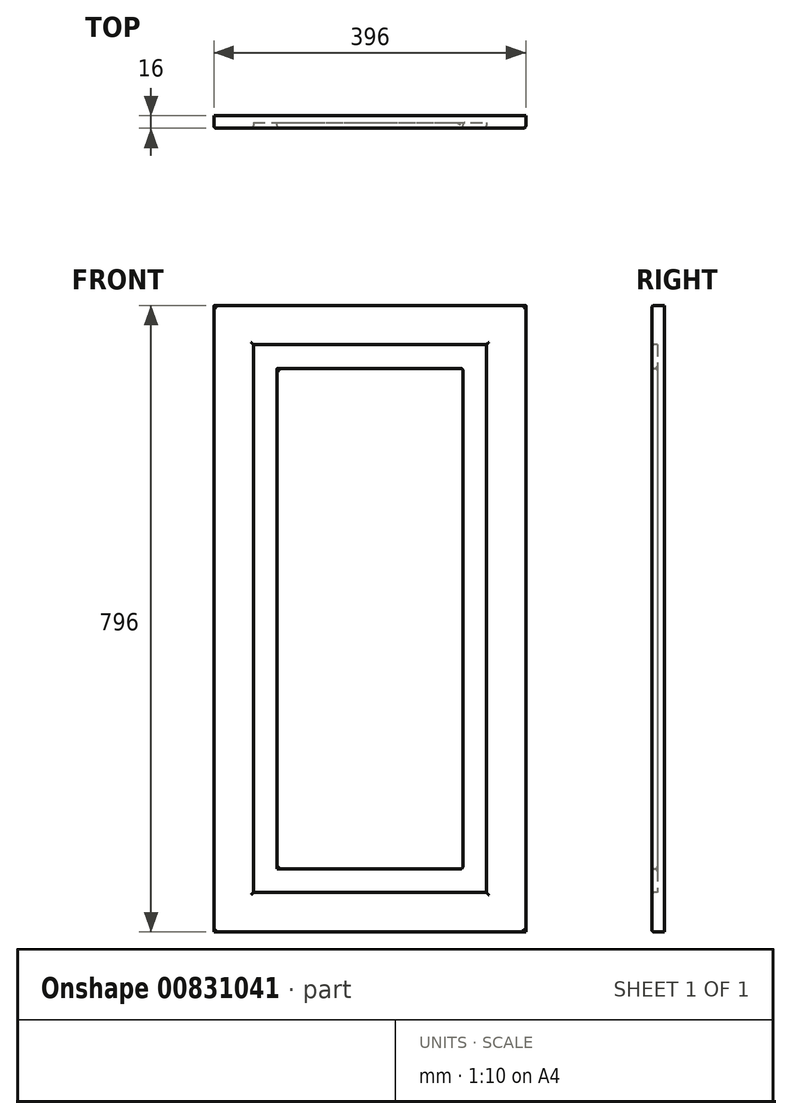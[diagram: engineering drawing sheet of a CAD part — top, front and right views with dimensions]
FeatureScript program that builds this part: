
annotation { "Feature Type Name" : "Feature", "Feature Type Description" : "" }
export const myFeature = defineFeature(function(context is Context, id is Id, definition is map)
    precondition{}
    {
        {
            var Q0;
            Q0=qCreatedBy(makeId("Front.planeOp"),FACE);
            var sketch = newSketch(context, id + "F0", { "sketchPlane" : qUnion([Q0])});
            skLineSegment(sketch, "E0.bottom", {"start": v(0, 0) * mm, "end": v(44.66, 0) * mm});
            skLineSegment(sketch, "E0.top", {"start": v(0, 33.8) * mm, "end": v(44.66, 33.8) * mm});
            skLineSegment(sketch, "E0.left", {"start": v(0, 0) * mm, "end": v(0, 33.8) * mm});
            skLineSegment(sketch, "E0.right", {"start": v(44.66, 0) * mm, "end": v(44.66, 33.8) * mm});
            skSolve(sketch);
        }
        {
            var Q0;
            Q0=makeQuery(id+"F0.imprint","IMPRINT",FACE,{"disambiguationData":[TD([[makeQuery(id+"F0.imprint","IMPRINT",EDGE,{"derivedFrom":sQuery(id+"F0.wireOp",EDGE,"E0.bottom")}),1.0]])]});
            extrude(context, id + "F1", {"entities" : qUnion([Q0]), "depth" : 16 * mm, "offsetDistance" : 25.4 * mm});
        }
        {
            var Q0;
            Q0=makeQuery(id+"F1.opExtrude","SWEPT_FACE",FACE,{"disambiguationData":[OSD([sQuery(id+"F0.wireOp",EDGE,"E0.bottom")])]});
            extrude(context, id + "F2", {"entities" : qUnion([Q0]), "operationType" : NewBodyOperationType.ADD, "oppositeDirection" : true, "depth" : 796 * mm, "offsetDistance" : 25 * mm});
        }
        {
            var Q0;
            {var subQ0=sQuery(id+"F0.wireOp",EDGE,"E0.left");Q0=makeQuery(id+"F2.boolean.opBoolean","MERGE",FACE,{"derivedFrom":[makeQuery(id+"F1.opExtrude","SWEPT_FACE",FACE,{"disambiguationData":[OSD([subQ0])]}),makeQuery(id+"F2.opExtrude","SWEPT_FACE",FACE,{"disambiguationData":[OSD([sQuery(id+"F0.wireOp",EDGE,"E0.bottom"),subQ0])]})]});}
            extrude(context, id + "F3", {"entities" : qUnion([Q0]), "operationType" : NewBodyOperationType.ADD, "oppositeDirection" : true, "depth" : 196 * mm, "offsetDistance" : 25 * mm});
        }
        {
            var Q0;
            {var subQ0=sQuery(id+"F0.wireOp",EDGE,"E0.left");var subQ1=sQuery(id+"F0.wireOp",EDGE,"E0.bottom");Q0=makeQuery(id+"F3.boolean.opBoolean","MERGE",FACE,{"derivedFrom":[makeQuery(id+"F2.boolean.opBoolean","MERGE",FACE,{"derivedFrom":[makeQuery(id+"F1.opExtrude","CAP_FACE",FACE,{"disambiguationData":[OSD([subQ1,sQuery(id+"F0.wireOp",EDGE,"E0.top"),subQ0,sQuery(id+"F0.wireOp",EDGE,"E0.right")])],"isStart":false}),makeQuery(id+"F2.opExtrude","SWEPT_FACE",FACE,{"disambiguationData":[OSD([subQ1]),TDD([makeQuery(id+"F1.opExtrude","CAP_EDGE",EDGE,{"disambiguationData":[OSD([subQ1])],"isStart":false})])]})]}),makeQuery(id+"F3.opExtrude","SWEPT_FACE",FACE,{"disambiguationData":[OSD([subQ1,subQ0]),TDD([makeQuery(id+"F2.boolean.opBoolean","MERGE",EDGE,{"derivedFrom":[makeQuery(id+"F1.opExtrude","CAP_EDGE",EDGE,{"disambiguationData":[OSD([subQ0])],"isStart":false}),makeQuery(id+"F2.opExtrude","SWEPT_EDGE",EDGE,{"disambiguationData":[OSD([subQ1,subQ0]),TDD([makeQuery(id+"F1.opExtrude","CAP_VERTEX",VERTEX,{"disambiguationData":[OSD([subQ1,subQ0])],"isStart":false})])]})]})])]})]});}
            var sketch = newSketch(context, id + "F4", { "sketchPlane" : qUnion([Q0])});
            skLineSegment(sketch, "E1.bottom", {"start": v(59.7, 646.67) * mm, "end": v(128.66, 646.67) * mm});
            skLineSegment(sketch, "E1.top", {"start": v(59.7, 152.97) * mm, "end": v(128.66, 152.97) * mm});
            skLineSegment(sketch, "E1.left", {"start": v(59.7, 646.67) * mm, "end": v(59.7, 152.97) * mm});
            skLineSegment(sketch, "E1.right", {"start": v(128.66, 646.67) * mm, "end": v(128.66, 152.97) * mm});
            skSolve(sketch);
        }
        {
            var Q0;
            Q0=makeQuery(id+"F4.imprint","IMPRINT",FACE,{"disambiguationData":[TD([[makeQuery(id+"F4.imprint","IMPRINT",EDGE,{"derivedFrom":sQuery(id+"F4.wireOp",EDGE,"E1.bottom")}),-1.0]])]});
            extrude(context, id + "F5", {"entities" : qUnion([Q0]), "operationType" : NewBodyOperationType.REMOVE, "oppositeDirection" : true, "depth" : 7 * mm, "offsetDistance" : 25 * mm});
        }
        {
            var Q0;
            Q0=makeQuery(id+"F5.boolean.opBoolean","COPY",FACE,{"derivedFrom":makeQuery(id+"F5.opExtrude","SWEPT_FACE",FACE,{"disambiguationData":[OSD([sQuery(id+"F4.wireOp",EDGE,"E1.left")])]})});
            extrude(context, id + "F6", {"entities" : qUnion([Q0]), "operationType" : NewBodyOperationType.REMOVE, "oppositeDirection" : true, "depth" : 9.7 * mm, "offsetDistance" : 25 * mm});
        }
        {
            var Q0;
            {var subQ0=sQuery(id+"F4.wireOp",EDGE,"E1.bottom");Q0=makeQuery(id+"F6.boolean.opBoolean","MERGE",FACE,{"derivedFrom":[makeQuery(id+"F5.boolean.opBoolean","COPY",FACE,{"derivedFrom":makeQuery(id+"F5.opExtrude","SWEPT_FACE",FACE,{"disambiguationData":[OSD([subQ0])]})}),makeQuery(id+"F6.opExtrude","SWEPT_FACE",FACE,{"disambiguationData":[OSD([subQ0,sQuery(id+"F4.wireOp",EDGE,"E1.left")])]})]});}
            extrude(context, id + "F7", {"entities" : qUnion([Q0]), "operationType" : NewBodyOperationType.ADD, "oppositeDirection" : true, "depth" : 99.33 * mm, "offsetDistance" : 25 * mm});
        }
        {
            var Q0;
            {var subQ0=sQuery(id+"F4.wireOp",EDGE,"E1.bottom");Q0=makeQuery(id+"F6.boolean.opBoolean","MERGE",FACE,{"derivedFrom":[makeQuery(id+"F5.boolean.opBoolean","COPY",FACE,{"derivedFrom":makeQuery(id+"F5.opExtrude","SWEPT_FACE",FACE,{"disambiguationData":[OSD([subQ0])]})}),makeQuery(id+"F6.opExtrude","SWEPT_FACE",FACE,{"disambiguationData":[OSD([subQ0,sQuery(id+"F4.wireOp",EDGE,"E1.left")])]})]});}
            extrude(context, id + "F8", {"entities" : qUnion([Q0]), "operationType" : NewBodyOperationType.REMOVE, "oppositeDirection" : true, "depth" : 99.33 * mm, "offsetDistance" : 25 * mm});
        }
        {
            var Q0;
            {var subQ0=sQuery(id+"F4.wireOp",EDGE,"E1.right");Q0=makeQuery(id+"F8.boolean.opBoolean","MERGE",FACE,{"derivedFrom":[makeQuery(id+"F5.boolean.opBoolean","COPY",FACE,{"derivedFrom":makeQuery(id+"F5.opExtrude","SWEPT_FACE",FACE,{"disambiguationData":[OSD([subQ0])]})}),makeQuery(id+"F8.opExtrude","SWEPT_FACE",FACE,{"disambiguationData":[OSD([sQuery(id+"F4.wireOp",EDGE,"E1.bottom"),subQ0])]})]});}
            extrude(context, id + "F9", {"entities" : qUnion([Q0]), "operationType" : NewBodyOperationType.REMOVE, "oppositeDirection" : true, "depth" : 17.34 * mm, "offsetDistance" : 25 * mm});
        }
        {
            var Q0;
            {var subQ0=sQuery(id+"F4.wireOp",EDGE,"E1.top");Q0=makeQuery(id+"F9.boolean.opBoolean","MERGE",FACE,{"derivedFrom":[makeQuery(id+"F6.boolean.opBoolean","MERGE",FACE,{"derivedFrom":[makeQuery(id+"F5.boolean.opBoolean","COPY",FACE,{"derivedFrom":makeQuery(id+"F5.opExtrude","SWEPT_FACE",FACE,{"disambiguationData":[OSD([subQ0])]})}),makeQuery(id+"F6.opExtrude","SWEPT_FACE",FACE,{"disambiguationData":[OSD([subQ0,sQuery(id+"F4.wireOp",EDGE,"E1.left")])]})]}),makeQuery(id+"F9.opExtrude","SWEPT_FACE",FACE,{"disambiguationData":[OSD([subQ0,sQuery(id+"F4.wireOp",EDGE,"E1.right")])]})]});}
            extrude(context, id + "F10", {"entities" : qUnion([Q0]), "operationType" : NewBodyOperationType.REMOVE, "oppositeDirection" : true, "depth" : 102.97 * mm, "offsetDistance" : 25 * mm});
        }
        {
            var Q0;
            {var subQ0=sQuery(id+"F4.wireOp",EDGE,"E1.right");var subQ1=sQuery(id+"F4.wireOp",EDGE,"E1.top");var subQ2=sQuery(id+"F4.wireOp",EDGE,"E1.left");var subQ3=sQuery(id+"F4.wireOp",EDGE,"E1.bottom");Q0=makeQuery(id+"F10.boolean.opBoolean","MERGE",FACE,{"derivedFrom":[makeQuery(id+"F9.boolean.opBoolean","MERGE",FACE,{"derivedFrom":[makeQuery(id+"F8.boolean.opBoolean","MERGE",FACE,{"derivedFrom":[makeQuery(id+"F6.boolean.opBoolean","MERGE",FACE,{"derivedFrom":[makeQuery(id+"F5.boolean.opBoolean","COPY",FACE,{"derivedFrom":makeQuery(id+"F5.opExtrude","CAP_FACE",FACE,{"disambiguationData":[OSD([subQ3,subQ1,subQ2,subQ0])],"isStart":false})}),makeQuery(id+"F6.opExtrude","SWEPT_FACE",FACE,{"disambiguationData":[OSD([subQ2]),TDD([makeQuery(id+"F5.boolean.opBoolean","COPY",EDGE,{"derivedFrom":makeQuery(id+"F5.opExtrude","CAP_EDGE",EDGE,{"disambiguationData":[OSD([subQ2])],"isStart":false})})])]})]}),makeQuery(id+"F8.opExtrude","SWEPT_FACE",FACE,{"disambiguationData":[OSD([subQ3,subQ2]),TDD([makeQuery(id+"F6.boolean.opBoolean","MERGE",EDGE,{"derivedFrom":[makeQuery(id+"F5.boolean.opBoolean","COPY",EDGE,{"derivedFrom":makeQuery(id+"F5.opExtrude","CAP_EDGE",EDGE,{"disambiguationData":[OSD([subQ3])],"isStart":false})}),makeQuery(id+"F6.opExtrude","SWEPT_EDGE",EDGE,{"disambiguationData":[OSD([subQ3,subQ2]),TDD([makeQuery(id+"F5.boolean.opBoolean","COPY",VERTEX,{"derivedFrom":makeQuery(id+"F5.opExtrude","CAP_VERTEX",VERTEX,{"disambiguationData":[OSD([subQ3,subQ2])],"isStart":false})})])]})]})])]})]}),makeQuery(id+"F9.opExtrude","SWEPT_FACE",FACE,{"disambiguationData":[OSD([subQ3,subQ0]),TDD([makeQuery(id+"F8.boolean.opBoolean","MERGE",EDGE,{"derivedFrom":[makeQuery(id+"F5.boolean.opBoolean","COPY",EDGE,{"derivedFrom":makeQuery(id+"F5.opExtrude","CAP_EDGE",EDGE,{"disambiguationData":[OSD([subQ0])],"isStart":false})}),makeQuery(id+"F8.opExtrude","SWEPT_EDGE",EDGE,{"disambiguationData":[OSD([subQ3,subQ0]),TDD([makeQuery(id+"F5.boolean.opBoolean","COPY",VERTEX,{"derivedFrom":makeQuery(id+"F5.opExtrude","CAP_VERTEX",VERTEX,{"disambiguationData":[OSD([subQ3,subQ0])],"isStart":false})})])]})]})])]})]}),makeQuery(id+"F10.opExtrude","SWEPT_FACE",FACE,{"disambiguationData":[OSD([subQ1,subQ2,subQ0]),TDD([makeQuery(id+"F9.boolean.opBoolean","MERGE",EDGE,{"derivedFrom":[makeQuery(id+"F6.boolean.opBoolean","MERGE",EDGE,{"derivedFrom":[makeQuery(id+"F5.boolean.opBoolean","COPY",EDGE,{"derivedFrom":makeQuery(id+"F5.opExtrude","CAP_EDGE",EDGE,{"disambiguationData":[OSD([subQ1])],"isStart":false})}),makeQuery(id+"F6.opExtrude","SWEPT_EDGE",EDGE,{"disambiguationData":[OSD([subQ1,subQ2]),TDD([makeQuery(id+"F5.boolean.opBoolean","COPY",VERTEX,{"derivedFrom":makeQuery(id+"F5.opExtrude","CAP_VERTEX",VERTEX,{"disambiguationData":[OSD([subQ1,subQ2])],"isStart":false})})])]})]}),makeQuery(id+"F9.opExtrude","SWEPT_EDGE",EDGE,{"disambiguationData":[OSD([subQ1,subQ0]),TDD([makeQuery(id+"F5.boolean.opBoolean","COPY",VERTEX,{"derivedFrom":makeQuery(id+"F5.opExtrude","CAP_VERTEX",VERTEX,{"disambiguationData":[OSD([subQ1,subQ0])],"isStart":false})})])]})]})])]})]});}
            var sketch = newSketch(context, id + "F11", { "sketchPlane" : qUnion([Q0])});
            skLineSegment(sketch, "E2.bottom", {"start": v(74.13, 678.73) * mm, "end": v(109.41, 678.73) * mm});
            skLineSegment(sketch, "E2.top", {"start": v(74.13, 186.63) * mm, "end": v(109.41, 186.63) * mm});
            skLineSegment(sketch, "E2.left", {"start": v(74.13, 678.73) * mm, "end": v(74.13, 186.63) * mm});
            skLineSegment(sketch, "E2.right", {"start": v(109.41, 678.73) * mm, "end": v(109.41, 186.63) * mm});
            skSolve(sketch);
        }
        {
            var Q0;
            Q0=makeQuery(id+"F11.imprint","IMPRINT",FACE,{"disambiguationData":[TD([[makeQuery(id+"F11.imprint","IMPRINT",EDGE,{"derivedFrom":sQuery(id+"F11.wireOp",EDGE,"E2.bottom")}),-1.0]])]});
            extrude(context, id + "F12", {"entities" : qUnion([Q0]), "operationType" : NewBodyOperationType.ADD, "depth" : 7 * mm, "offsetDistance" : 25 * mm});
        }
        {
            var Q0;
            Q0=makeQuery(id+"F12.opExtrude","SWEPT_FACE",FACE,{"disambiguationData":[OSD([sQuery(id+"F11.wireOp",EDGE,"E2.bottom")])]});
            extrude(context, id + "F13", {"entities" : qUnion([Q0]), "operationType" : NewBodyOperationType.ADD, "depth" : 37.27 * mm, "offsetDistance" : 25 * mm});
        }
        {
            var Q0;
            {var subQ0=sQuery(id+"F11.wireOp",EDGE,"E2.right");Q0=makeQuery(id+"F13.boolean.opBoolean","MERGE",FACE,{"derivedFrom":[makeQuery(id+"F12.opExtrude","SWEPT_FACE",FACE,{"disambiguationData":[OSD([subQ0])]}),makeQuery(id+"F13.opExtrude","SWEPT_FACE",FACE,{"disambiguationData":[OSD([sQuery(id+"F11.wireOp",EDGE,"E2.bottom"),subQ0])]})]});}
            extrude(context, id + "F14", {"entities" : qUnion([Q0]), "operationType" : NewBodyOperationType.ADD, "depth" : 6.58 * mm, "offsetDistance" : 25 * mm});
        }
        {
            var Q0;
            {var subQ0=sQuery(id+"F11.wireOp",EDGE,"E2.top");Q0=makeQuery(id+"F14.boolean.opBoolean","MERGE",FACE,{"derivedFrom":[makeQuery(id+"F12.opExtrude","SWEPT_FACE",FACE,{"disambiguationData":[OSD([subQ0])]}),makeQuery(id+"F14.opExtrude","SWEPT_FACE",FACE,{"disambiguationData":[OSD([subQ0,sQuery(id+"F11.wireOp",EDGE,"E2.right")])]})]});}
            extrude(context, id + "F15", {"entities" : qUnion([Q0]), "operationType" : NewBodyOperationType.ADD, "depth" : 106.63 * mm, "offsetDistance" : 25 * mm});
        }
        {
            var Q0;
            {var subQ0=sQuery(id+"F11.wireOp",EDGE,"E2.left");Q0=makeQuery(id+"F15.boolean.opBoolean","MERGE",FACE,{"derivedFrom":[makeQuery(id+"F13.boolean.opBoolean","MERGE",FACE,{"derivedFrom":[makeQuery(id+"F12.opExtrude","SWEPT_FACE",FACE,{"disambiguationData":[OSD([subQ0])]}),makeQuery(id+"F13.opExtrude","SWEPT_FACE",FACE,{"disambiguationData":[OSD([sQuery(id+"F11.wireOp",EDGE,"E2.bottom"),subQ0])]})]}),makeQuery(id+"F15.opExtrude","SWEPT_FACE",FACE,{"disambiguationData":[OSD([sQuery(id+"F11.wireOp",EDGE,"E2.top"),subQ0])]})]});}
            extrude(context, id + "F16", {"entities" : qUnion([Q0]), "operationType" : NewBodyOperationType.REMOVE, "oppositeDirection" : true, "depth" : 5.87 * mm, "offsetDistance" : 25 * mm});
        }
        {
            var Q0;
            Q0=makeQuery(id+"F3.opExtrude","CAP_FACE",FACE,{"disambiguationData":[OSD([sQuery(id+"F0.wireOp",EDGE,"E0.bottom"),sQuery(id+"F0.wireOp",EDGE,"E0.left")])],"isStart":false});
            extrude(context, id + "F17", {"entities" : qUnion([Q0]), "operationType" : NewBodyOperationType.ADD, "depth" : 200 * mm, "offsetDistance" : 25 * mm});
        }
        {
            var Q0;
            {var subQ0=sQuery(id+"F4.wireOp",EDGE,"E1.right");Q0=makeQuery(id+"F10.boolean.opBoolean","MERGE",FACE,{"derivedFrom":[makeQuery(id+"F9.boolean.opBoolean","COPY",FACE,{"derivedFrom":makeQuery(id+"F9.opExtrude","CAP_FACE",FACE,{"disambiguationData":[OSD([sQuery(id+"F4.wireOp",EDGE,"E1.bottom"),subQ0])],"isStart":false})}),makeQuery(id+"F10.opExtrude","SWEPT_FACE",FACE,{"disambiguationData":[OSD([sQuery(id+"F4.wireOp",EDGE,"E1.top"),subQ0])]})]});}
            extrude(context, id + "F18", {"entities" : qUnion([Q0]), "operationType" : NewBodyOperationType.REMOVE, "oppositeDirection" : true, "depth" : 200 * mm, "offsetDistance" : 25 * mm});
        }
        {
            var Q0;
            {var subQ0=sQuery(id+"F11.wireOp",EDGE,"E2.right");var subQ1=sQuery(id+"F11.wireOp",EDGE,"E2.top");Q0=makeQuery(id+"F15.boolean.opBoolean","MERGE",FACE,{"derivedFrom":[makeQuery(id+"F14.opExtrude","CAP_FACE",FACE,{"disambiguationData":[OSD([sQuery(id+"F11.wireOp",EDGE,"E2.bottom"),subQ0])],"isStart":false}),makeQuery(id+"F15.opExtrude","SWEPT_FACE",FACE,{"disambiguationData":[OSD([subQ1,subQ0]),TDD([makeQuery(id+"F14.opExtrude","CAP_EDGE",EDGE,{"disambiguationData":[OSD([subQ1,subQ0])],"isStart":false})])]})]});}
            extrude(context, id + "F19", {"entities" : qUnion([Q0]), "operationType" : NewBodyOperationType.ADD, "depth" : 200 * mm, "offsetDistance" : 25 * mm});
        }
        {
            var Q0;
            {var subQ0=sQuery(id+"F11.wireOp",EDGE,"E2.right");var subQ1=sQuery(id+"F11.wireOp",EDGE,"E2.top");Q0=makeQuery(id+"F19.boolean.opBoolean","MERGE",FACE,{"derivedFrom":[makeQuery(id+"F15.opExtrude","CAP_FACE",FACE,{"disambiguationData":[OSD([subQ1,subQ0])],"isStart":false}),makeQuery(id+"F19.opExtrude","SWEPT_FACE",FACE,{"disambiguationData":[OSD([subQ1,subQ0])]})]});}
            extrude(context, id + "F20", {"entities" : qUnion([Q0]), "operationType" : NewBodyOperationType.REMOVE, "oppositeDirection" : true, "depth" : 600 * mm, "offsetDistance" : 25 * mm});
        }
        {
            var Q0;
            {var subQ0=sQuery(id+"F4.wireOp",EDGE,"E1.right");var subQ1=sQuery(id+"F4.wireOp",EDGE,"E1.top");Q0=makeQuery(id+"F18.boolean.opBoolean","MERGE",FACE,{"derivedFrom":[makeQuery(id+"F10.boolean.opBoolean","COPY",FACE,{"derivedFrom":makeQuery(id+"F10.opExtrude","CAP_FACE",FACE,{"disambiguationData":[OSD([subQ1,sQuery(id+"F4.wireOp",EDGE,"E1.left"),subQ0])],"isStart":false})}),makeQuery(id+"F18.opExtrude","SWEPT_FACE",FACE,{"disambiguationData":[OSD([subQ1,subQ0])]})]});}
            extrude(context, id + "F21", {"entities" : qUnion([Q0]), "operationType" : NewBodyOperationType.ADD, "depth" : 600 * mm, "offsetDistance" : 25 * mm});
        }
        {
            var Q0;
            {var subQ0=sQuery(id+"F0.wireOp",EDGE,"E0.left");var subQ1=sQuery(id+"F0.wireOp",EDGE,"E0.bottom");var subQ2=makeQuery(id+"F1.opExtrude","SWEPT_EDGE",EDGE,{"disambiguationData":[OSD([subQ1,subQ0])]});Q0=makeQuery(id+"F17.boolean.opBoolean","MERGE",FACE,{"derivedFrom":[makeQuery(id+"F3.boolean.opBoolean","MERGE",FACE,{"derivedFrom":[makeQuery(id+"F1.opExtrude","SWEPT_FACE",FACE,{"disambiguationData":[OSD([subQ1])]}),makeQuery(id+"F3.opExtrude","SWEPT_FACE",FACE,{"disambiguationData":[OSD([subQ1,subQ0]),TDD([subQ2])]})]}),makeQuery(id+"F17.opExtrude","SWEPT_FACE",FACE,{"disambiguationData":[OSD([subQ1,subQ0]),TDD([makeQuery(id+"F3.opExtrude","CAP_EDGE",EDGE,{"disambiguationData":[OSD([subQ1,subQ0]),TDD([subQ2])],"isStart":false})])]})]});}
            extrude(context, id + "F22", {"entities" : qUnion([Q0]), "operationType" : NewBodyOperationType.REMOVE, "oppositeDirection" : true, "depth" : 600 * mm, "offsetDistance" : 25 * mm});
        }
        {
            var Q0;
            Q0=makeQuery(id+"F22.boolean.opBoolean","COPY",FACE,{"derivedFrom":makeQuery(id+"F22.opExtrude","CAP_FACE",FACE,{"disambiguationData":[OSD([sQuery(id+"F0.wireOp",EDGE,"E0.bottom"),sQuery(id+"F0.wireOp",EDGE,"E0.left")])],"isStart":false})});
            extrude(context, id + "F23", {"entities" : qUnion([Q0]), "operationType" : NewBodyOperationType.ADD, "depth" : 200 * mm, "offsetDistance" : 25 * mm});
        }
        {
            var Q0;
            Q0=makeQuery(id+"F21.opExtrude","CAP_FACE",FACE,{"disambiguationData":[OSD([sQuery(id+"F4.wireOp",EDGE,"E1.top"),sQuery(id+"F4.wireOp",EDGE,"E1.left"),sQuery(id+"F4.wireOp",EDGE,"E1.right")])],"isStart":false});
            extrude(context, id + "F24", {"entities" : qUnion([Q0]), "operationType" : NewBodyOperationType.REMOVE, "oppositeDirection" : true, "depth" : 200 * mm, "offsetDistance" : 25 * mm});
        }
        {
            var Q0;
            Q0=makeQuery(id+"F20.boolean.opBoolean","COPY",FACE,{"derivedFrom":makeQuery(id+"F20.opExtrude","CAP_FACE",FACE,{"disambiguationData":[OSD([sQuery(id+"F11.wireOp",EDGE,"E2.top"),sQuery(id+"F11.wireOp",EDGE,"E2.right")])],"isStart":false})});
            extrude(context, id + "F25", {"entities" : qUnion([Q0]), "operationType" : NewBodyOperationType.ADD, "depth" : 200 * mm, "offsetDistance" : 25 * mm});
        }
        {
            var Q0;
            {var subQ0=sQuery(id+"F0.wireOp",EDGE,"E0.left");var subQ1=sQuery(id+"F0.wireOp",EDGE,"E0.bottom");var subQ2=makeQuery(id+"F2.opExtrude","CAP_EDGE",EDGE,{"disambiguationData":[OSD([subQ1,subQ0])],"isStart":false});Q0=makeQuery(id+"F17.boolean.opBoolean","MERGE",FACE,{"derivedFrom":[makeQuery(id+"F3.boolean.opBoolean","MERGE",FACE,{"derivedFrom":[makeQuery(id+"F2.opExtrude","CAP_FACE",FACE,{"disambiguationData":[OSD([subQ1])],"isStart":false}),makeQuery(id+"F3.opExtrude","SWEPT_FACE",FACE,{"disambiguationData":[OSD([subQ1,subQ0]),TDD([subQ2])]})]}),makeQuery(id+"F17.opExtrude","SWEPT_FACE",FACE,{"disambiguationData":[OSD([subQ1,subQ0]),TDD([makeQuery(id+"F3.opExtrude","CAP_EDGE",EDGE,{"disambiguationData":[OSD([subQ1,subQ0]),TDD([subQ2])],"isStart":false})])]})]});}
            extrude(context, id + "F26", {"entities" : qUnion([Q0]), "operationType" : NewBodyOperationType.ADD, "depth" : 200 * mm, "offsetDistance" : 25 * mm});
        }
        {
            var Q0;
            {var subQ0=sQuery(id+"F4.wireOp",EDGE,"E1.right");var subQ1=sQuery(id+"F4.wireOp",EDGE,"E1.bottom");Q0=makeQuery(id+"F18.boolean.opBoolean","MERGE",FACE,{"derivedFrom":[makeQuery(id+"F9.boolean.opBoolean","MERGE",FACE,{"derivedFrom":[makeQuery(id+"F8.boolean.opBoolean","COPY",FACE,{"derivedFrom":makeQuery(id+"F8.opExtrude","CAP_FACE",FACE,{"disambiguationData":[OSD([subQ1,sQuery(id+"F4.wireOp",EDGE,"E1.left")])],"isStart":false})}),makeQuery(id+"F9.opExtrude","SWEPT_FACE",FACE,{"disambiguationData":[OSD([subQ1,subQ0]),TDD([makeQuery(id+"F8.boolean.opBoolean","COPY",EDGE,{"derivedFrom":makeQuery(id+"F8.opExtrude","CAP_EDGE",EDGE,{"disambiguationData":[OSD([subQ1,subQ0])],"isStart":false})})])]})]}),makeQuery(id+"F18.opExtrude","SWEPT_FACE",FACE,{"disambiguationData":[OSD([subQ1,subQ0])]})]});}
            extrude(context, id + "F27", {"entities" : qUnion([Q0]), "operationType" : NewBodyOperationType.REMOVE, "oppositeDirection" : true, "depth" : 200 * mm, "offsetDistance" : 25 * mm});
        }
        {
            var Q0;
            {var subQ0=sQuery(id+"F11.wireOp",EDGE,"E2.right");var subQ1=sQuery(id+"F11.wireOp",EDGE,"E2.bottom");Q0=makeQuery(id+"F19.boolean.opBoolean","MERGE",FACE,{"derivedFrom":[makeQuery(id+"F14.boolean.opBoolean","MERGE",FACE,{"derivedFrom":[makeQuery(id+"F13.opExtrude","CAP_FACE",FACE,{"disambiguationData":[OSD([subQ1])],"isStart":false}),makeQuery(id+"F14.opExtrude","SWEPT_FACE",FACE,{"disambiguationData":[OSD([subQ1,subQ0]),TDD([makeQuery(id+"F13.opExtrude","CAP_EDGE",EDGE,{"disambiguationData":[OSD([subQ1,subQ0])],"isStart":false})])]})]}),makeQuery(id+"F19.opExtrude","SWEPT_FACE",FACE,{"disambiguationData":[OSD([subQ1,subQ0])]})]});}
            extrude(context, id + "F28", {"entities" : qUnion([Q0]), "operationType" : NewBodyOperationType.ADD, "depth" : 200 * mm, "offsetDistance" : 25 * mm});
        }
        {
            var Q0;
            Q0=makeQuery(id+"F23.opExtrude","CAP_FACE",FACE,{"disambiguationData":[OSD([sQuery(id+"F0.wireOp",EDGE,"E0.bottom"),sQuery(id+"F0.wireOp",EDGE,"E0.left")])],"isStart":false});
            extrude(context, id + "F29", {"entities" : qUnion([Q0]), "operationType" : NewBodyOperationType.ADD, "depth" : 200 * mm, "offsetDistance" : 25 * mm});
        }
        {
            var Q0;
            Q0=makeQuery(id+"F24.boolean.opBoolean","COPY",FACE,{"derivedFrom":makeQuery(id+"F24.opExtrude","CAP_FACE",FACE,{"disambiguationData":[OSD([sQuery(id+"F4.wireOp",EDGE,"E1.top"),sQuery(id+"F4.wireOp",EDGE,"E1.left"),sQuery(id+"F4.wireOp",EDGE,"E1.right")])],"isStart":false})});
            extrude(context, id + "F30", {"entities" : qUnion([Q0]), "operationType" : NewBodyOperationType.REMOVE, "oppositeDirection" : true, "depth" : 200 * mm, "offsetDistance" : 25 * mm});
        }
        {
            var Q0;
            Q0=makeQuery(id+"F25.opExtrude","CAP_FACE",FACE,{"disambiguationData":[OSD([sQuery(id+"F11.wireOp",EDGE,"E2.top"),sQuery(id+"F11.wireOp",EDGE,"E2.right")])],"isStart":false});
            extrude(context, id + "F31", {"entities" : qUnion([Q0]), "operationType" : NewBodyOperationType.ADD, "depth" : 200 * mm, "offsetDistance" : 25 * mm});
        }
        {
            var Q0;
            {var subQ0=sQuery(id+"F0.wireOp",EDGE,"E0.left");var subQ1=sQuery(id+"F0.wireOp",EDGE,"E0.bottom");var subQ2=makeQuery(id+"F1.opExtrude","CAP_VERTEX",VERTEX,{"disambiguationData":[OSD([subQ1,subQ0])],"isStart":false});var subQ3=makeQuery(id+"F1.opExtrude","CAP_EDGE",EDGE,{"disambiguationData":[OSD([subQ1])],"isStart":false});var subQ4=makeQuery(id+"F22.boolean.opBoolean","COPY",EDGE,{"derivedFrom":makeQuery(id+"F22.opExtrude","CAP_EDGE",EDGE,{"disambiguationData":[OSD([subQ1,subQ0]),TDD([makeQuery(id+"F17.boolean.opBoolean","MERGE",EDGE,{"derivedFrom":[makeQuery(id+"F3.boolean.opBoolean","MERGE",EDGE,{"derivedFrom":[subQ3,makeQuery(id+"F3.opExtrude","SWEPT_EDGE",EDGE,{"disambiguationData":[OSD([subQ1,subQ0]),TDD([subQ2])]})]}),makeQuery(id+"F17.opExtrude","SWEPT_EDGE",EDGE,{"disambiguationData":[OSD([subQ1,subQ0]),TDD([makeQuery(id+"F3.opExtrude","CAP_VERTEX",VERTEX,{"disambiguationData":[OSD([subQ1,subQ0]),TDD([subQ2])],"isStart":false})])]})]})])],"isStart":false})});var subQ5=makeQuery(id+"F2.opExtrude","CAP_VERTEX",VERTEX,{"disambiguationData":[OSD([subQ1,subQ0]),TDD([subQ2])],"isStart":false});var subQ6=sQuery(id+"F4.wireOp",EDGE,"E1.right");var subQ7=sQuery(id+"F4.wireOp",EDGE,"E1.top");var subQ8=makeQuery(id+"F5.boolean.opBoolean","COPY",VERTEX,{"derivedFrom":makeQuery(id+"F5.opExtrude","CAP_VERTEX",VERTEX,{"disambiguationData":[OSD([subQ7,subQ6])],"isStart":true})});var subQ9=sQuery(id+"F4.wireOp",EDGE,"E1.left");var subQ10=makeQuery(id+"F2.boolean.opBoolean","MERGE",EDGE,{"derivedFrom":[makeQuery(id+"F1.opExtrude","CAP_EDGE",EDGE,{"disambiguationData":[OSD([subQ0])],"isStart":false}),makeQuery(id+"F2.opExtrude","SWEPT_EDGE",EDGE,{"disambiguationData":[OSD([subQ1,subQ0]),TDD([subQ2])]})]});Q0=makeQuery(id+"F29.boolean.opBoolean","MERGE",FACE,{"derivedFrom":[makeQuery(id+"F26.boolean.opBoolean","MERGE",FACE,{"derivedFrom":[makeQuery(id+"F23.boolean.opBoolean","MERGE",FACE,{"derivedFrom":[makeQuery(id+"F21.boolean.opBoolean","MERGE",FACE,{"derivedFrom":[makeQuery(id+"F17.boolean.opBoolean","MERGE",FACE,{"derivedFrom":[makeQuery(id+"F3.boolean.opBoolean","MERGE",FACE,{"derivedFrom":[makeQuery(id+"F2.boolean.opBoolean","MERGE",FACE,{"derivedFrom":[makeQuery(id+"F1.opExtrude","CAP_FACE",FACE,{"disambiguationData":[OSD([subQ1,sQuery(id+"F0.wireOp",EDGE,"E0.top"),subQ0,sQuery(id+"F0.wireOp",EDGE,"E0.right")])],"isStart":false}),makeQuery(id+"F2.opExtrude","SWEPT_FACE",FACE,{"disambiguationData":[OSD([subQ1]),TDD([subQ3])]})]}),makeQuery(id+"F3.opExtrude","SWEPT_FACE",FACE,{"disambiguationData":[OSD([subQ1,subQ0]),TDD([subQ10])]})]}),makeQuery(id+"F17.opExtrude","SWEPT_FACE",FACE,{"disambiguationData":[OSD([subQ1,subQ0]),TDD([makeQuery(id+"F3.opExtrude","CAP_EDGE",EDGE,{"disambiguationData":[OSD([subQ1,subQ0]),TDD([subQ10])],"isStart":false})])]})]}),makeQuery(id+"F21.opExtrude","SWEPT_FACE",FACE,{"disambiguationData":[OSD([subQ7,subQ9,subQ6]),TDD([makeQuery(id+"F18.boolean.opBoolean","MERGE",EDGE,{"derivedFrom":[makeQuery(id+"F10.boolean.opBoolean","COPY",EDGE,{"derivedFrom":makeQuery(id+"F10.opExtrude","CAP_EDGE",EDGE,{"disambiguationData":[OSD([subQ7,subQ9,subQ6]),TDD([makeQuery(id+"F9.boolean.opBoolean","MERGE",EDGE,{"derivedFrom":[makeQuery(id+"F6.boolean.opBoolean","MERGE",EDGE,{"derivedFrom":[makeQuery(id+"F5.boolean.opBoolean","COPY",EDGE,{"derivedFrom":makeQuery(id+"F5.opExtrude","CAP_EDGE",EDGE,{"disambiguationData":[OSD([subQ7])],"isStart":true})}),makeQuery(id+"F6.opExtrude","SWEPT_EDGE",EDGE,{"disambiguationData":[OSD([subQ7,subQ9]),TDD([makeQuery(id+"F5.boolean.opBoolean","COPY",VERTEX,{"derivedFrom":makeQuery(id+"F5.opExtrude","CAP_VERTEX",VERTEX,{"disambiguationData":[OSD([subQ7,subQ9])],"isStart":true})})])]})]}),makeQuery(id+"F9.opExtrude","SWEPT_EDGE",EDGE,{"disambiguationData":[OSD([subQ7,subQ6]),TDD([subQ8])]})]})])],"isStart":false})}),makeQuery(id+"F18.opExtrude","SWEPT_EDGE",EDGE,{"disambiguationData":[OSD([subQ7,subQ6]),TDD([makeQuery(id+"F10.boolean.opBoolean","COPY",VERTEX,{"derivedFrom":makeQuery(id+"F10.opExtrude","CAP_VERTEX",VERTEX,{"disambiguationData":[OSD([subQ7,subQ6]),TDD([makeQuery(id+"F9.boolean.opBoolean","COPY",VERTEX,{"derivedFrom":makeQuery(id+"F9.opExtrude","CAP_VERTEX",VERTEX,{"disambiguationData":[OSD([subQ7,subQ6]),TDD([subQ8])],"isStart":false})})])],"isStart":false})})])]})]})])]})]}),makeQuery(id+"F23.opExtrude","SWEPT_FACE",FACE,{"disambiguationData":[OSD([subQ1,subQ0]),TDD([subQ4])]})]}),makeQuery(id+"F26.opExtrude","SWEPT_FACE",FACE,{"disambiguationData":[OSD([subQ1,subQ0]),TDD([makeQuery(id+"F17.boolean.opBoolean","MERGE",EDGE,{"derivedFrom":[makeQuery(id+"F3.boolean.opBoolean","MERGE",EDGE,{"derivedFrom":[makeQuery(id+"F2.opExtrude","CAP_EDGE",EDGE,{"disambiguationData":[OSD([subQ1]),TDD([subQ3])],"isStart":false}),makeQuery(id+"F3.opExtrude","SWEPT_EDGE",EDGE,{"disambiguationData":[OSD([subQ1,subQ0]),TDD([subQ5])]})]}),makeQuery(id+"F17.opExtrude","SWEPT_EDGE",EDGE,{"disambiguationData":[OSD([subQ1,subQ0]),TDD([makeQuery(id+"F3.opExtrude","CAP_VERTEX",VERTEX,{"disambiguationData":[OSD([subQ1,subQ0]),TDD([subQ5])],"isStart":false})])]})]})])]})]}),makeQuery(id+"F29.opExtrude","SWEPT_FACE",FACE,{"disambiguationData":[OSD([subQ1,subQ0]),TDD([makeQuery(id+"F23.opExtrude","CAP_EDGE",EDGE,{"disambiguationData":[OSD([subQ1,subQ0]),TDD([subQ4])],"isStart":false})])]})]});}
            var Q1;
            {var subQ0=sQuery(id+"F11.wireOp",EDGE,"E2.right");var subQ1=sQuery(id+"F11.wireOp",EDGE,"E2.top");var subQ2=makeQuery(id+"F12.opExtrude","CAP_VERTEX",VERTEX,{"disambiguationData":[OSD([subQ1,subQ0])],"isStart":false});var subQ3=makeQuery(id+"F14.opExtrude","CAP_VERTEX",VERTEX,{"disambiguationData":[OSD([subQ1,subQ0]),TDD([subQ2])],"isStart":false});var subQ4=makeQuery(id+"F14.boolean.opBoolean","MERGE",EDGE,{"derivedFrom":[makeQuery(id+"F12.opExtrude","CAP_EDGE",EDGE,{"disambiguationData":[OSD([subQ1])],"isStart":false}),makeQuery(id+"F14.opExtrude","SWEPT_EDGE",EDGE,{"disambiguationData":[OSD([subQ1,subQ0]),TDD([subQ2])]})]});var subQ5=makeQuery(id+"F20.boolean.opBoolean","COPY",EDGE,{"derivedFrom":makeQuery(id+"F20.opExtrude","CAP_EDGE",EDGE,{"disambiguationData":[OSD([subQ1,subQ0]),TDD([makeQuery(id+"F19.boolean.opBoolean","MERGE",EDGE,{"derivedFrom":[makeQuery(id+"F15.opExtrude","CAP_EDGE",EDGE,{"disambiguationData":[OSD([subQ1,subQ0]),TDD([subQ4])],"isStart":false}),makeQuery(id+"F19.opExtrude","SWEPT_EDGE",EDGE,{"disambiguationData":[OSD([subQ1,subQ0]),TDD([makeQuery(id+"F15.opExtrude","CAP_VERTEX",VERTEX,{"disambiguationData":[OSD([subQ1,subQ0]),TDD([subQ3])],"isStart":false})])]})]})])],"isStart":false})});var subQ6=sQuery(id+"F11.wireOp",EDGE,"E2.bottom");var subQ7=makeQuery(id+"F12.opExtrude","CAP_VERTEX",VERTEX,{"disambiguationData":[OSD([subQ6,subQ0])],"isStart":false});var subQ8=makeQuery(id+"F13.opExtrude","CAP_VERTEX",VERTEX,{"disambiguationData":[OSD([subQ6,subQ0]),TDD([subQ7])],"isStart":false});var subQ9=makeQuery(id+"F12.opExtrude","CAP_EDGE",EDGE,{"disambiguationData":[OSD([subQ6])],"isStart":false});var subQ10=makeQuery(id+"F13.boolean.opBoolean","MERGE",EDGE,{"derivedFrom":[makeQuery(id+"F12.opExtrude","CAP_EDGE",EDGE,{"disambiguationData":[OSD([subQ0])],"isStart":false}),makeQuery(id+"F13.opExtrude","SWEPT_EDGE",EDGE,{"disambiguationData":[OSD([subQ6,subQ0]),TDD([subQ7])]})]});Q1=makeQuery(id+"F31.boolean.opBoolean","MERGE",FACE,{"derivedFrom":[makeQuery(id+"F28.boolean.opBoolean","MERGE",FACE,{"derivedFrom":[makeQuery(id+"F25.boolean.opBoolean","MERGE",FACE,{"derivedFrom":[makeQuery(id+"F19.boolean.opBoolean","MERGE",FACE,{"derivedFrom":[makeQuery(id+"F15.boolean.opBoolean","MERGE",FACE,{"derivedFrom":[makeQuery(id+"F14.boolean.opBoolean","MERGE",FACE,{"derivedFrom":[makeQuery(id+"F13.boolean.opBoolean","MERGE",FACE,{"derivedFrom":[makeQuery(id+"F12.opExtrude","CAP_FACE",FACE,{"disambiguationData":[OSD([subQ6,subQ1,sQuery(id+"F11.wireOp",EDGE,"E2.left"),subQ0])],"isStart":false}),makeQuery(id+"F13.opExtrude","SWEPT_FACE",FACE,{"disambiguationData":[OSD([subQ6]),TDD([subQ9])]})]}),makeQuery(id+"F14.opExtrude","SWEPT_FACE",FACE,{"disambiguationData":[OSD([subQ6,subQ0]),TDD([subQ10])]})]}),makeQuery(id+"F15.opExtrude","SWEPT_FACE",FACE,{"disambiguationData":[OSD([subQ1,subQ0]),TDD([subQ4])]})]}),makeQuery(id+"F19.opExtrude","SWEPT_FACE",FACE,{"disambiguationData":[OSD([subQ6,subQ1,subQ0]),TDD([makeQuery(id+"F15.boolean.opBoolean","MERGE",EDGE,{"derivedFrom":[makeQuery(id+"F14.opExtrude","CAP_EDGE",EDGE,{"disambiguationData":[OSD([subQ6,subQ0]),TDD([subQ10])],"isStart":false}),makeQuery(id+"F15.opExtrude","SWEPT_EDGE",EDGE,{"disambiguationData":[OSD([subQ1,subQ0]),TDD([subQ3])]})]})])]})]}),makeQuery(id+"F25.opExtrude","SWEPT_FACE",FACE,{"disambiguationData":[OSD([subQ1,subQ0]),TDD([subQ5])]})]}),makeQuery(id+"F28.opExtrude","SWEPT_FACE",FACE,{"disambiguationData":[OSD([subQ6,subQ0]),TDD([makeQuery(id+"F19.boolean.opBoolean","MERGE",EDGE,{"derivedFrom":[makeQuery(id+"F14.boolean.opBoolean","MERGE",EDGE,{"derivedFrom":[makeQuery(id+"F13.opExtrude","CAP_EDGE",EDGE,{"disambiguationData":[OSD([subQ6]),TDD([subQ9])],"isStart":false}),makeQuery(id+"F14.opExtrude","SWEPT_EDGE",EDGE,{"disambiguationData":[OSD([subQ6,subQ0]),TDD([subQ8])]})]}),makeQuery(id+"F19.opExtrude","SWEPT_EDGE",EDGE,{"disambiguationData":[OSD([subQ6,subQ0]),TDD([makeQuery(id+"F14.opExtrude","CAP_VERTEX",VERTEX,{"disambiguationData":[OSD([subQ6,subQ0]),TDD([subQ8])],"isStart":false})])]})]})])]})]}),makeQuery(id+"F31.opExtrude","SWEPT_FACE",FACE,{"disambiguationData":[OSD([subQ1,subQ0]),TDD([makeQuery(id+"F25.opExtrude","CAP_EDGE",EDGE,{"disambiguationData":[OSD([subQ1,subQ0]),TDD([subQ5])],"isStart":false})])]})]});}
            fillet(context, id + "F32", {"entities" : qUnion([Q0, Q1]), "radius" : 3 * mm, "tangentPropagation" : true, "allowEdgeOverflow" : false});
        }
    });
